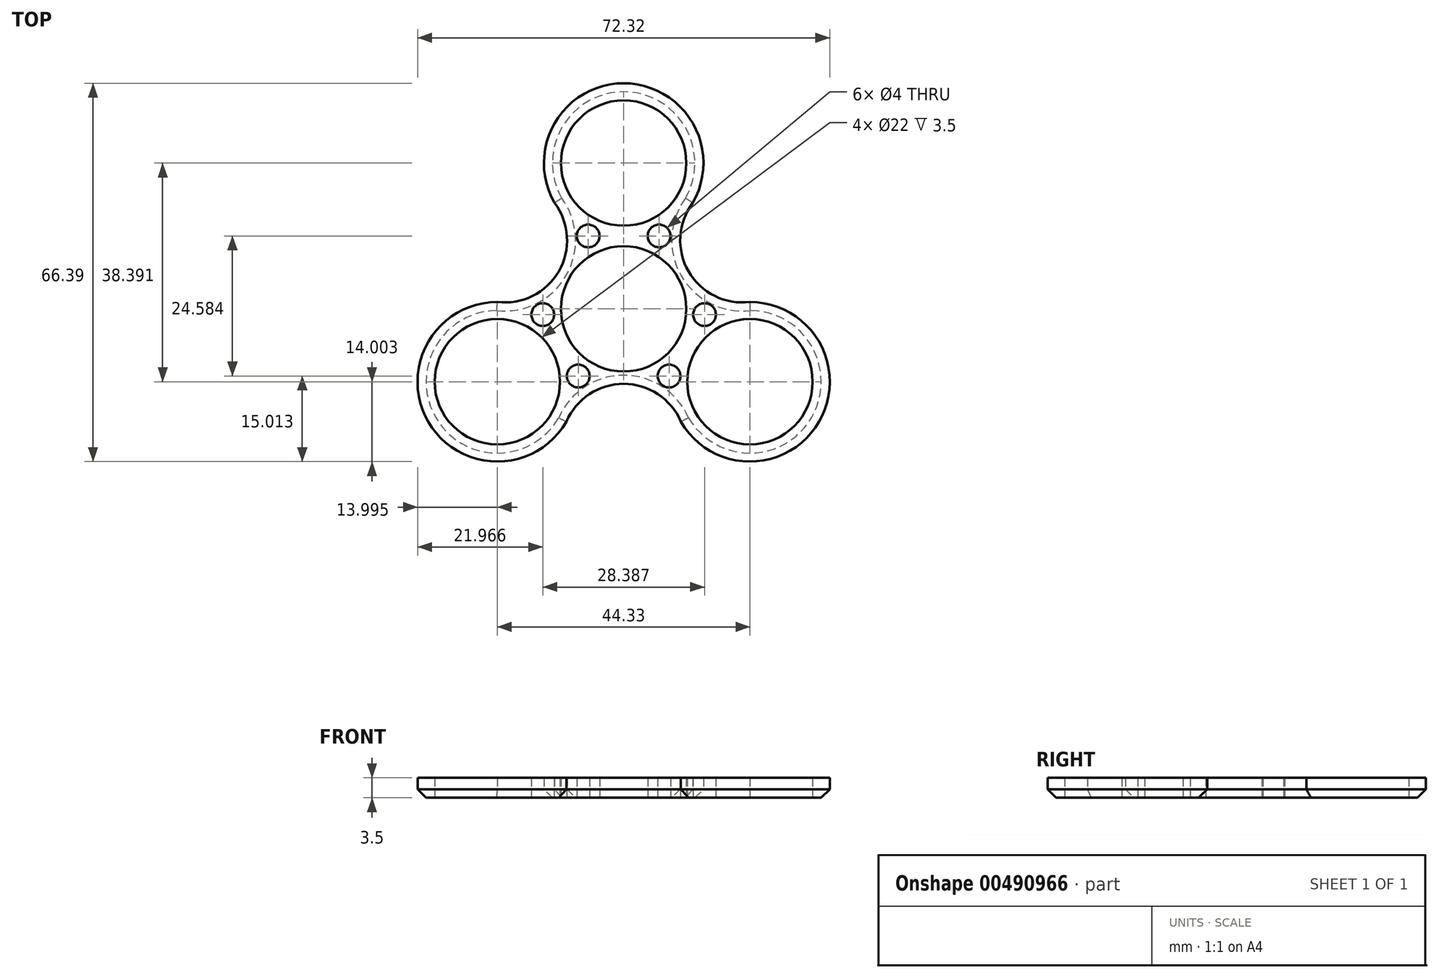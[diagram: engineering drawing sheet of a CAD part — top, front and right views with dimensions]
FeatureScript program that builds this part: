
annotation { "Feature Type Name" : "Feature", "Feature Type Description" : "" }
export const myFeature = defineFeature(function(context is Context, id is Id, definition is map)
    precondition{}
    {
        {
            var Q0;
            Q0=qCreatedBy(makeId("Top.planeOp"),FACE);
            var sketch = newSketch(context, id + "F0", { "sketchPlane" : qUnion([Q0])});
            skCircle(sketch, "E0", {"center": v(0, 0) * mm, "radius": 11 * mm});
            skCircle(sketch, "E1", {"center": v(0, 25.6) * mm, "radius": 11 * mm});
            skArc(sketch, "E2.0", {"start": v(12.12, 18.6) * mm, "mid": v(0, 39.6) * mm, "end": v(-12.12, 18.6) * mm});
            skLineSegment(sketch, "E3", {"start": v(0, 25.6) * mm, "end": v(-9.53, 20.1) * mm});
            skLineSegment(sketch, "E4.MirrorCS", {"start": v(0, 25.6) * mm, "end": v(9.53, 20.1) * mm});
            skArc(sketch, "E5.1.0", {"start": v(-22.16, 1.2) * mm, "mid": v(-34.29, -19.8) * mm, "end": v(-10.04, -19.8) * mm});
            skCircle(sketch, "E5.1.1", {"center": v(-22.16, -12.8) * mm, "radius": 11 * mm});
            skArc(sketch, "E5.2.0", {"start": v(10.04, -19.8) * mm, "mid": v(34.29, -19.8) * mm, "end": v(22.16, 1.2) * mm});
            skCircle(sketch, "E5.2.1", {"center": v(22.16, -12.8) * mm, "radius": 11 * mm});
            skArc(sketch, "E6", {"start": v(-22.16, 1.2) * mm, "mid": v(-11.4, 6.58) * mm, "end": v(-12.12, 18.6) * mm});
            skArc(sketch, "E7.1.0", {"start": v(10.04, -19.8) * mm, "mid": v(0, -13.15) * mm, "end": v(-10.04, -19.8) * mm});
            skArc(sketch, "E7.2.0", {"start": v(12.12, 18.6) * mm, "mid": v(11.4, 6.58) * mm, "end": v(22.16, 1.2) * mm});
            skLineSegment(sketch, "E8", {"start": v(0, 11) * mm, "end": v(0, 14.6) * mm});
            skLineSegment(sketch, "E9", {"start": v(-4.98, 12.8) * mm, "end": v(-7.47, 12.8) * mm});
            skPoint(sketch, "E10", {"position": v(-4.98, 12.8) * mm});
            skPoint(sketch, "E11.orphan", {"position": v(0, 12.8) * mm});
            skPoint(sketch, "E12", {"position": v(-7.47, 12.8) * mm});
            skPoint(sketch, "E13.orphan", {"position": v(-9.96, 12.8) * mm});
            skPoint(sketch, "E14", {"position": v(-6.22, 12.8) * mm});
            skCircle(sketch, "E15", {"center": v(-6.22, 12.8) * mm, "radius": 2 * mm});
            skCircle(sketch, "E16.MirrorC", {"center": v(6.22, 12.8) * mm, "radius": 2 * mm});
            skCircle(sketch, "E17.1.0", {"center": v(-7.97, -11.79) * mm, "radius": 2 * mm});
            skCircle(sketch, "E17.1.1", {"center": v(-14.2, -1) * mm, "radius": 2 * mm});
            skCircle(sketch, "E17.2.0", {"center": v(14.2, -1) * mm, "radius": 2 * mm});
            skCircle(sketch, "E17.2.1", {"center": v(7.97, -11.79) * mm, "radius": 2 * mm});
            skSolve(sketch);
        }
        {
            var Q0;
            Q0=makeQuery(id+"F0.imprint","IMPRINT",FACE,{"disambiguationData":[TD([[makeQuery(id+"F0.imprint","IMPRINT",EDGE,{"derivedFrom":sQuery(id+"F0.wireOp",EDGE,"E0")}),-1.0]])]});
            extrude(context, id + "F1", {"entities" : qUnion([Q0]), "depth" : 3.5 * mm});
        }
        {
            var Q0;
            Q0=makeQuery(id+"F1.opExtrude","CAP_EDGE",EDGE,{"disambiguationData":[OSD([sQuery(id+"F0.wireOp",EDGE,"E5.1.0")])],"isStart":true});
            var Q1;
            Q1=makeQuery(id+"F1.opExtrude","CAP_EDGE",EDGE,{"disambiguationData":[OSD([sQuery(id+"F0.wireOp",EDGE,"E7.1.0")])],"isStart":true});
            var Q2;
            Q2=makeQuery(id+"F1.opExtrude","CAP_EDGE",EDGE,{"disambiguationData":[OSD([sQuery(id+"F0.wireOp",EDGE,"E5.2.0")])],"isStart":true});
            var Q3;
            Q3=makeQuery(id+"F1.opExtrude","CAP_EDGE",EDGE,{"disambiguationData":[OSD([sQuery(id+"F0.wireOp",EDGE,"E7.2.0")])],"isStart":true});
            var Q4;
            Q4=makeQuery(id+"F1.opExtrude","CAP_EDGE",EDGE,{"disambiguationData":[OSD([sQuery(id+"F0.wireOp",EDGE,"E2.0")])],"isStart":true});
            var Q5;
            Q5=makeQuery(id+"F1.opExtrude","CAP_EDGE",EDGE,{"disambiguationData":[OSD([sQuery(id+"F0.wireOp",EDGE,"E6")])],"isStart":true});
            chamfer(context, id + "F2", {"entities" : qUnion([Q0, Q1, Q2, Q3, Q4, Q5]), "width" : 1.5 * mm, "tangentPropagation" : true});
        }
    });
